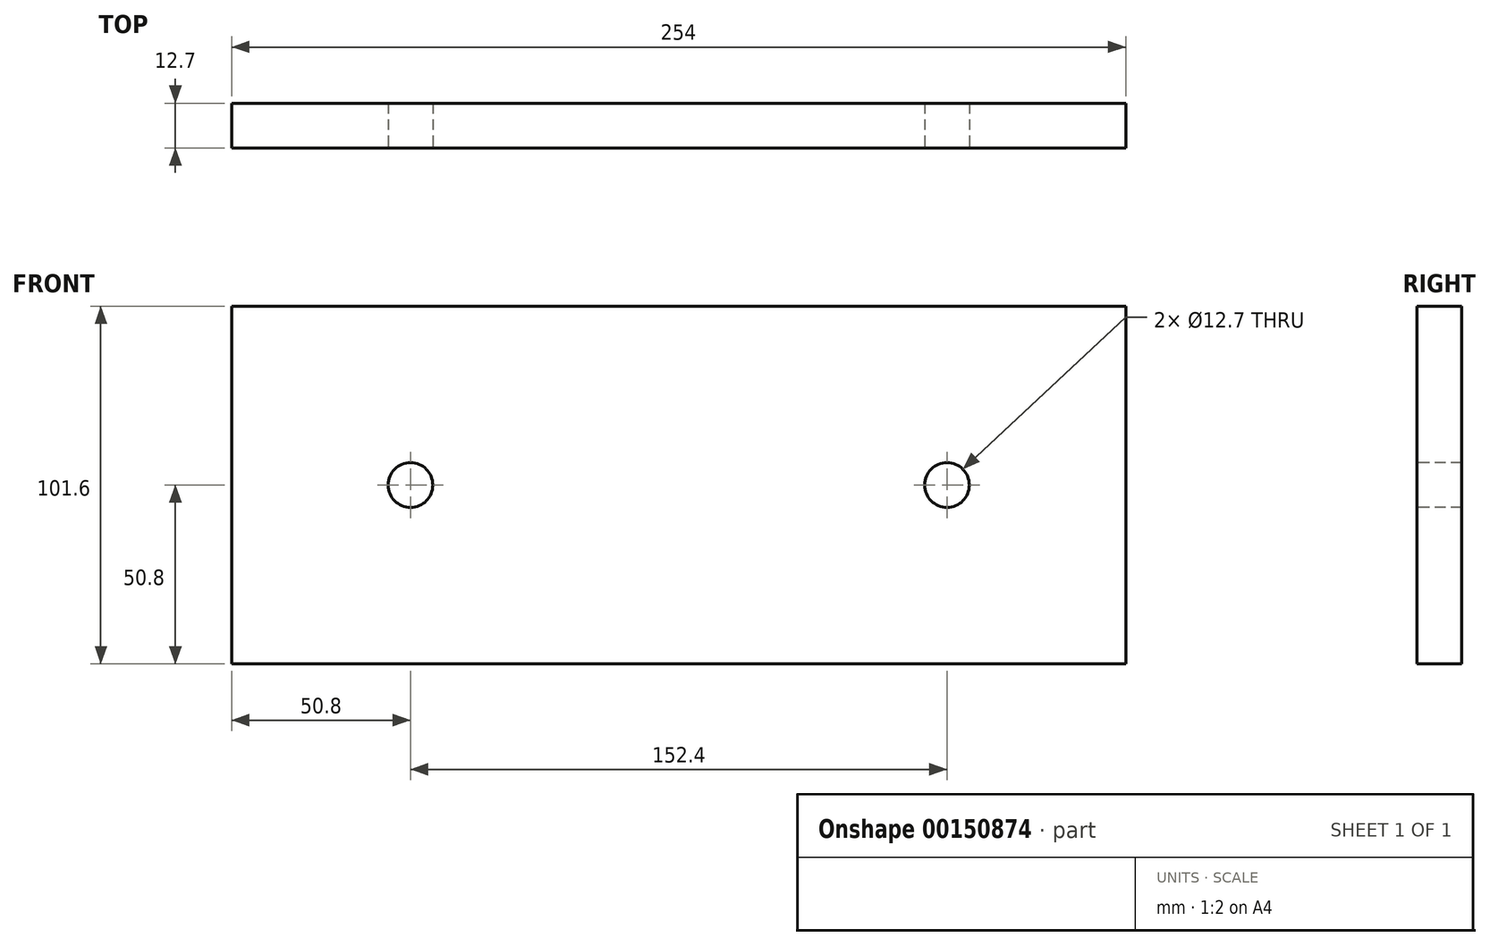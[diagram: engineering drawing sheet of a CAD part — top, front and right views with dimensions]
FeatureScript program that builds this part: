
annotation { "Feature Type Name" : "Feature", "Feature Type Description" : "" }
export const myFeature = defineFeature(function(context is Context, id is Id, definition is map)
    precondition{}
    {
        {
            var Q0;
            Q0=qCreatedBy(makeId("Front.planeOp"),FACE);
            var sketch = newSketch(context, id + "F0", { "sketchPlane" : qUnion([Q0])});
            skLineSegment(sketch, "E0.bottom", {"start": v(0, 0) * mm, "end": v(254, 0) * mm});
            skLineSegment(sketch, "E0.top", {"start": v(0, 101.6) * mm, "end": v(254, 101.6) * mm});
            skLineSegment(sketch, "E0.left", {"start": v(0, 0) * mm, "end": v(0, 101.6) * mm});
            skLineSegment(sketch, "E0.right", {"start": v(254, 0) * mm, "end": v(254, 101.6) * mm});
            skSolve(sketch);
        }
        {
            var Q0;
            Q0 = qSketchRegion(id + "F0", true);
            extrude(context, id + "F1", {"entities" : qUnion([Q0]), "depth" : 12.7 * mm});
        }
        {
            var Q0;
            Q0=makeQuery(id+"F1.opExtrude","CAP_FACE",FACE,{"disambiguationData":[OSD([sQuery(id+"F0.wireOp",EDGE,"E0.bottom"),sQuery(id+"F0.wireOp",EDGE,"E0.top"),sQuery(id+"F0.wireOp",EDGE,"E0.left"),sQuery(id+"F0.wireOp",EDGE,"E0.right")])],"isStart":false});
            var sketch = newSketch(context, id + "F2", { "sketchPlane" : qUnion([Q0])});
            skCircle(sketch, "E1", {"center": v(50.8, 50.8) * mm, "radius": 6.35 * mm});
            skPoint(sketch, "E1.centerSnap0", {"position": v(0, 50.8) * mm});
            skCircle(sketch, "E2", {"center": v(203.2, 50.8) * mm, "radius": 6.35 * mm});
            skSolve(sketch);
        }
        {
            var Q0;
            Q0 = qSketchRegion(id + "F2", true);
            extrude(context, id + "F3", {"entities" : qUnion([Q0]), "operationType" : NewBodyOperationType.REMOVE, "endBound" : BoundingType.THROUGH_ALL, "oppositeDirection" : true, "depth" : 25.4 * mm});
        }
    });
